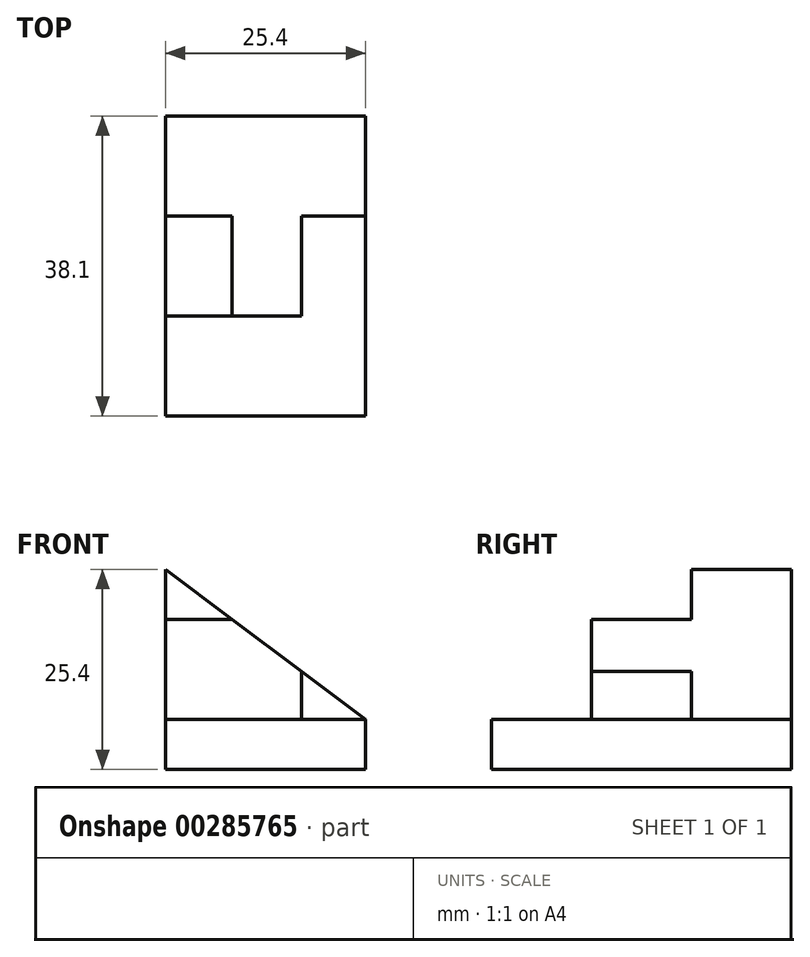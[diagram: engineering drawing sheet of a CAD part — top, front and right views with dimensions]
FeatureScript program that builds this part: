
annotation { "Feature Type Name" : "Feature", "Feature Type Description" : "" }
export const myFeature = defineFeature(function(context is Context, id is Id, definition is map)
    precondition{}
    {
        {
            var Q0;
            Q0=qCreatedBy(makeId("Top.planeOp"),FACE);
            var sketch = newSketch(context, id + "F0", { "sketchPlane" : qUnion([Q0])});
            skLineSegment(sketch, "E0.bottom", {"start": v(0, 0) * mm, "end": v(25.4, 0) * mm});
            skLineSegment(sketch, "E0.top", {"start": v(0, 38.1) * mm, "end": v(25.4, 38.1) * mm});
            skLineSegment(sketch, "E0.left", {"start": v(0, 0) * mm, "end": v(0, 38.1) * mm});
            skLineSegment(sketch, "E0.right", {"start": v(25.4, 0) * mm, "end": v(25.4, 38.1) * mm});
            skSolve(sketch);
        }
        {
            var Q0;
            Q0=makeQuery(id+"F0.imprint","IMPRINT",FACE,{"disambiguationData":[TD([[makeQuery(id+"F0.imprint","IMPRINT",EDGE,{"derivedFrom":sQuery(id+"F0.wireOp",EDGE,"E0.bottom")}),1.0]])]});
            extrude(context, id + "F1", {"entities" : qUnion([Q0]), "depth" : 25.4 * mm});
        }
        {
            var Q0;
            Q0=qCreatedBy(makeId("Front.planeOp"),FACE);
            var sketch = newSketch(context, id + "F2", { "sketchPlane" : qUnion([Q0])});
            skLineSegment(sketch, "E1", {"start": v(0, 25.4) * mm, "end": v(25.4, 6.35) * mm});
            skLineSegment(sketch, "E2", {"start": v(0, 25.4) * mm, "end": v(25.4, 25.4) * mm});
            skLineSegment(sketch, "E3", {"start": v(25.4, 25.4) * mm, "end": v(25.4, 6.35) * mm});
            skSolve(sketch);
        }
        {
            var Q0;
            Q0 = qSketchRegion(id + "F2", true);
            extrude(context, id + "F3", {"entities" : qUnion([Q0]), "operationType" : NewBodyOperationType.REMOVE, "oppositeDirection" : true, "depth" : 50.8 * mm});
        }
        {
            var Q0;
            Q0=qCreatedBy(makeId("Right.planeOp"),FACE);
            var sketch = newSketch(context, id + "F4", { "sketchPlane" : qUnion([Q0])});
            skLineSegment(sketch, "E4.bottom", {"start": v(0, 6.35) * mm, "end": v(12.7, 6.35) * mm});
            skLineSegment(sketch, "E4.top", {"start": v(0, 25.4) * mm, "end": v(12.7, 25.4) * mm});
            skLineSegment(sketch, "E4.left", {"start": v(0, 6.35) * mm, "end": v(0, 25.4) * mm});
            skLineSegment(sketch, "E4.right", {"start": v(12.7, 6.35) * mm, "end": v(12.7, 25.4) * mm});
            skSolve(sketch);
        }
        {
            var Q0;
            Q0 = qSketchRegion(id + "F4", true);
            extrude(context, id + "F5", {"entities" : qUnion([Q0]), "operationType" : NewBodyOperationType.REMOVE, "depth" : 50.8 * mm});
        }
        {
            var Q0;
            Q0=qCreatedBy(makeId("Top.planeOp"),FACE);
            var sketch = newSketch(context, id + "F6", { "sketchPlane" : qUnion([Q0])});
            skLineSegment(sketch, "E5.bottom", {"start": v(25.4, 12.7) * mm, "end": v(19.05, 12.7) * mm});
            skLineSegment(sketch, "E5.top", {"start": v(25.4, 25.4) * mm, "end": v(19.05, 25.4) * mm});
            skLineSegment(sketch, "E5.left", {"start": v(25.4, 12.7) * mm, "end": v(25.4, 25.4) * mm});
            skLineSegment(sketch, "E5.right", {"start": v(19.05, 12.7) * mm, "end": v(19.05, 25.4) * mm});
            skSolve(sketch);
        }
        {
            var Q0;
            Q0=qCreatedBy(makeId("Right.planeOp"),FACE);
            var sketch = newSketch(context, id + "F7", { "sketchPlane" : qUnion([Q0])});
            skLineSegment(sketch, "E6.bottom", {"start": v(25.4, 25.4) * mm, "end": v(12.7, 25.4) * mm});
            skLineSegment(sketch, "E6.top", {"start": v(25.4, 19.05) * mm, "end": v(12.7, 19.05) * mm});
            skLineSegment(sketch, "E6.left", {"start": v(25.4, 25.4) * mm, "end": v(25.4, 19.05) * mm});
            skLineSegment(sketch, "E6.right", {"start": v(12.7, 25.4) * mm, "end": v(12.7, 19.05) * mm});
            skSolve(sketch);
        }
        {
            var Q0;
            Q0 = qSketchRegion(id + "F7", true);
            extrude(context, id + "F8", {"entities" : qUnion([Q0]), "operationType" : NewBodyOperationType.REMOVE, "depth" : 25.4 * mm});
        }
        {
            var Q0;
            Q0=qCreatedBy(makeId("Front.planeOp"),FACE);
            var sketch = newSketch(context, id + "F9", { "sketchPlane" : qUnion([Q0])});
            skLineSegment(sketch, "E7.bottom", {"start": v(25.4, 6.35) * mm, "end": v(17.27, 6.35) * mm});
            skLineSegment(sketch, "E7.top", {"start": v(25.4, 12.7) * mm, "end": v(17.27, 12.7) * mm});
            skLineSegment(sketch, "E7.left", {"start": v(25.4, 6.35) * mm, "end": v(25.4, 12.7) * mm});
            skLineSegment(sketch, "E7.right", {"start": v(17.27, 6.35) * mm, "end": v(17.27, 12.7) * mm});
            skSolve(sketch);
        }
        {
            var Q0;
            Q0 = qSketchRegion(id + "F9", true);
            extrude(context, id + "F10", {"entities" : qUnion([Q0]), "operationType" : NewBodyOperationType.REMOVE, "oppositeDirection" : true, "depth" : 25.4 * mm});
        }
    });
